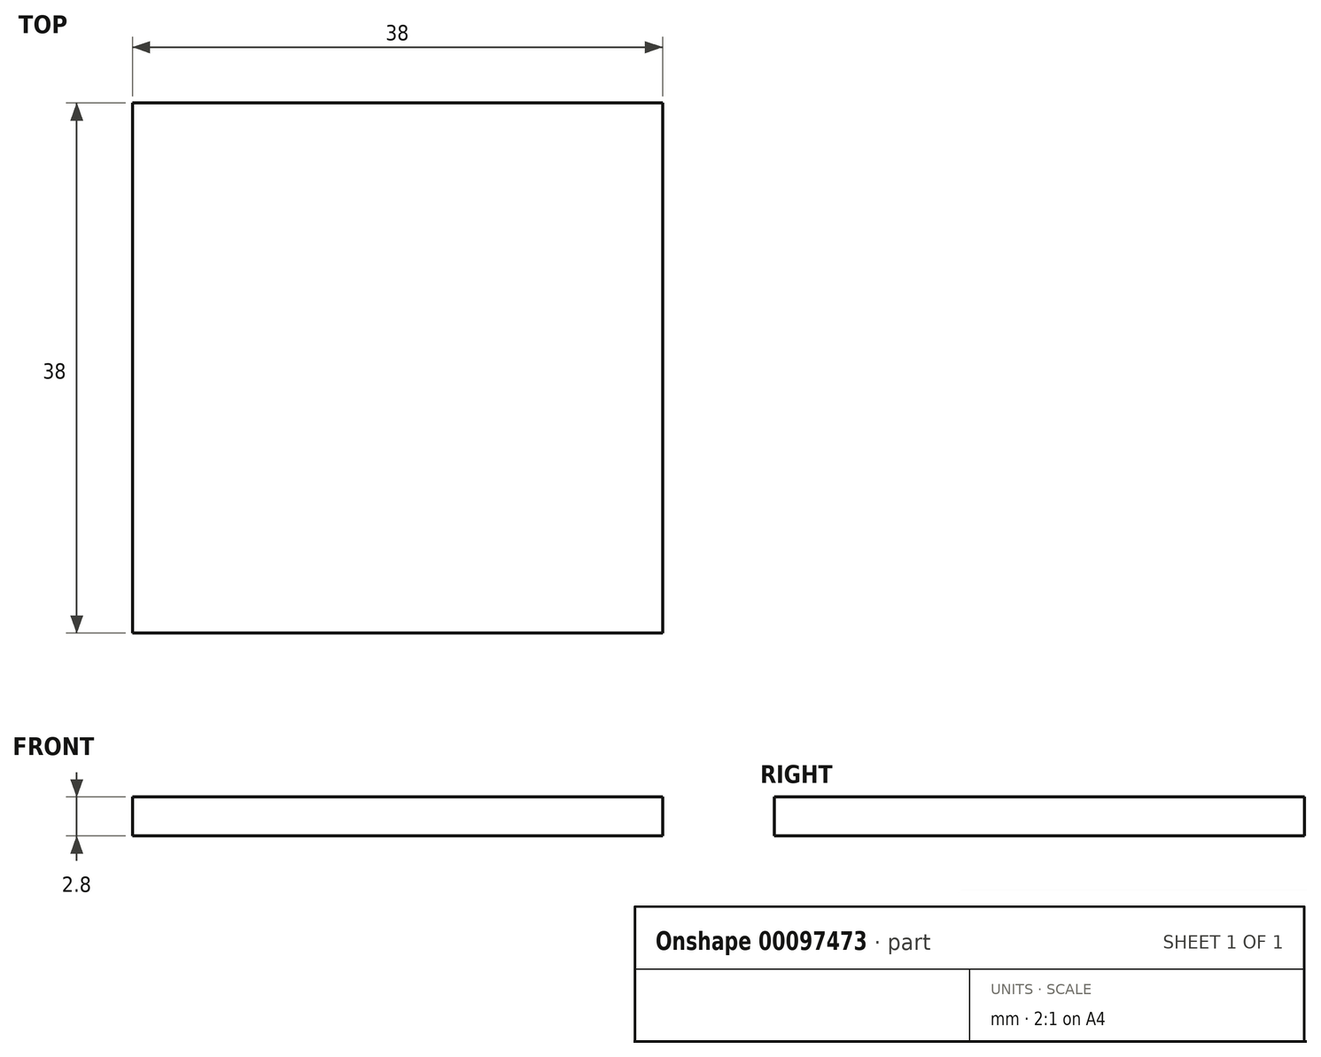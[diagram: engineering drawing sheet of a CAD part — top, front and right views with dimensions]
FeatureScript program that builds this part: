
annotation { "Feature Type Name" : "Feature", "Feature Type Description" : "" }
export const myFeature = defineFeature(function(context is Context, id is Id, definition is map)
    precondition{}
    {
        {
            var Q0;
            Q0=qCreatedBy(makeId("Top.planeOp"),FACE);
            var sketch = newSketch(context, id + "F0", { "sketchPlane" : qUnion([Q0])});
            skLineSegment(sketch, "E0.bottom", {"start": v(0, 0) * mm, "end": v(-38, 0) * mm});
            skLineSegment(sketch, "E0.top", {"start": v(0, 38) * mm, "end": v(-38, 38) * mm});
            skLineSegment(sketch, "E0.left", {"start": v(0, 0) * mm, "end": v(0, 38) * mm});
            skLineSegment(sketch, "E0.right", {"start": v(-38, 0) * mm, "end": v(-38, 38) * mm});
            skSolve(sketch);
        }
        {
            var Q0;
            Q0=makeQuery(id+"F0.imprint","IMPRINT",FACE,{"disambiguationData":[TD([[makeQuery(id+"F0.imprint","IMPRINT",EDGE,{"derivedFrom":sQuery(id+"F0.wireOp",EDGE,"E0.bottom")}),-1.0]])]});
            extrude(context, id + "F1", {"entities" : qUnion([Q0]), "depth" : 2.8 * mm});
        }
    });
